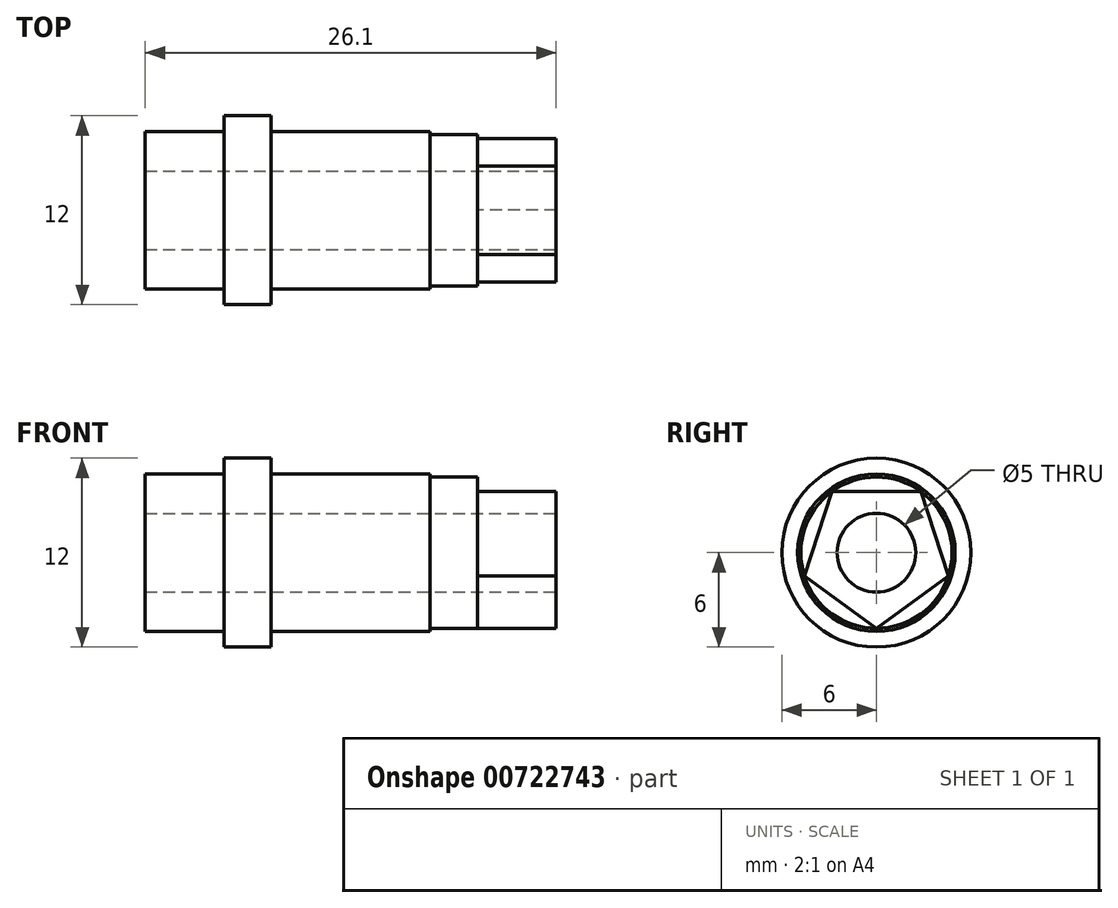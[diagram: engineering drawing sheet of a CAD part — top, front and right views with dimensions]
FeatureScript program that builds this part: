
annotation { "Feature Type Name" : "Feature", "Feature Type Description" : "" }
export const myFeature = defineFeature(function(context is Context, id is Id, definition is map)
    precondition{}
    {
        {
            var Q0;
            Q0=qCreatedBy(makeId("Right.planeOp"),FACE);
            var sketch = newSketch(context, id + "F0", { "sketchPlane" : qUnion([Q0])});
            skCircle(sketch, "E0", {"center": v(0, 0) * mm, "radius": 5 * mm});
            skSolve(sketch);
        }
        {
            var Q0;
            Q0=qSketchRegion(id+"F0",true);
            extrude(context, id + "F1", {"entities" : qUnion([Q0]), "oppositeDirection" : true, "depth" : 10.1 * mm, "offsetDistance" : 25 * mm});
        }
        {
            var Q0;
            Q0=makeQuery(id+"F1.opExtrude","CAP_FACE",FACE,{"disambiguationData":[OSD([sQuery(id+"F0.wireOp",EDGE,"E0")])],"isStart":true});
            var sketch = newSketch(context, id + "F2", { "sketchPlane" : qUnion([Q0])});
            skCircle(sketch, "E1", {"center": v(0, 0) * mm, "radius": 4.8 * mm});
            skSolve(sketch);
        }
        {
            var Q0;
            Q0=qSketchRegion(id+"F2",true);
            extrude(context, id + "F3", {"entities" : qUnion([Q0]), "operationType" : NewBodyOperationType.ADD, "depth" : 3 * mm, "offsetDistance" : 25 * mm});
        }
        {
            var Q0;
            Q0=makeQuery(id+"F3.opExtrude","CAP_FACE",FACE,{"disambiguationData":[OSD([sQuery(id+"F2.wireOp",EDGE,"E1")])],"isStart":false});
            var sketch = newSketch(context, id + "F4", { "sketchPlane" : qUnion([Q0])});
            skCircle(sketch, "E2.cCircle", {"center": v(0, 0) * mm, "radius": 4.8 * mm, "construction": true});
            skLineSegment(sketch, "E2.0", {"start": v(0, -4.8) * mm, "end": v(-4.57, -1.48) * mm});
            skLineSegment(sketch, "E2.1", {"start": v(-4.57, -1.48) * mm, "end": v(-2.82, 3.88) * mm});
            skLineSegment(sketch, "E2.2", {"start": v(-2.82, 3.88) * mm, "end": v(2.82, 3.88) * mm});
            skLineSegment(sketch, "E2.3", {"start": v(2.82, 3.88) * mm, "end": v(4.57, -1.48) * mm});
            skLineSegment(sketch, "E2.4", {"start": v(4.57, -1.48) * mm, "end": v(0, -4.8) * mm});
            skSolve(sketch);
        }
        {
            var Q0;
            Q0=qSketchRegion(id+"F4",true);
            extrude(context, id + "F5", {"entities" : qUnion([Q0]), "operationType" : NewBodyOperationType.ADD, "depth" : 5 * mm, "offsetDistance" : 25 * mm});
        }
        {
            var Q0;
            Q0=makeQuery(id+"F1.opExtrude","CAP_FACE",FACE,{"disambiguationData":[OSD([sQuery(id+"F0.wireOp",EDGE,"E0")])],"isStart":false});
            var sketch = newSketch(context, id + "F6", { "sketchPlane" : qUnion([Q0])});
            skCircle(sketch, "E3", {"center": v(0, 0) * mm, "radius": 6 * mm});
            skSolve(sketch);
        }
        {
            var Q0;
            Q0=qSketchRegion(id+"F6",true);
            extrude(context, id + "F7", {"entities" : qUnion([Q0]), "operationType" : NewBodyOperationType.ADD, "depth" : 3 * mm, "offsetDistance" : 25 * mm});
        }
        {
            var Q0;
            {var subQ0=sQuery(id+"F6.wireOp",EDGE,"E3");Q0=makeQuery(id+"F7.boolean.opBoolean","SPLIT",FACE,{"disambiguationData":[TD([makeQuery(id+"F5.opExtrude","SWEPT_FACE",FACE,{"disambiguationData":[OSD([sQuery(id+"F4.wireOp",EDGE,"E2.0")])]})])],"derivedFrom":makeQuery(id+"F7.opExtrude","CAP_FACE",FACE,{"disambiguationData":[OSD([subQ0])],"isStart":false})});}
            var sketch = newSketch(context, id + "F8", { "sketchPlane" : qUnion([Q0])});
            skCircle(sketch, "E4", {"center": v(0, 0) * mm, "radius": 5 * mm});
            skSolve(sketch);
        }
        {
            var Q0;
            Q0=qSketchRegion(id+"F8",true);
            extrude(context, id + "F9", {"entities" : qUnion([Q0]), "operationType" : NewBodyOperationType.ADD, "depth" : 5 * mm, "offsetDistance" : 25 * mm});
        }
        {
            var Q0;
            Q0=makeQuery(id+"F5.opExtrude","CAP_FACE",FACE,{"disambiguationData":[OSD([sQuery(id+"F4.wireOp",EDGE,"E2.0"),sQuery(id+"F4.wireOp",EDGE,"E2.1"),sQuery(id+"F4.wireOp",EDGE,"E2.2"),sQuery(id+"F4.wireOp",EDGE,"E2.3"),sQuery(id+"F4.wireOp",EDGE,"E2.4")])],"isStart":false});
            var sketch = newSketch(context, id + "F10", { "sketchPlane" : qUnion([Q0])});
            skCircle(sketch, "E5", {"center": v(0, 0) * mm, "radius": 2.5 * mm});
            skSolve(sketch);
        }
        {
            var Q0;
            Q0=qSketchRegion(id+"F10",true);
            extrude(context, id + "F11", {"entities" : qUnion([Q0]), "operationType" : NewBodyOperationType.REMOVE, "oppositeDirection" : true, "depth" : 80 * mm, "offsetDistance" : 25 * mm});
        }
    });
